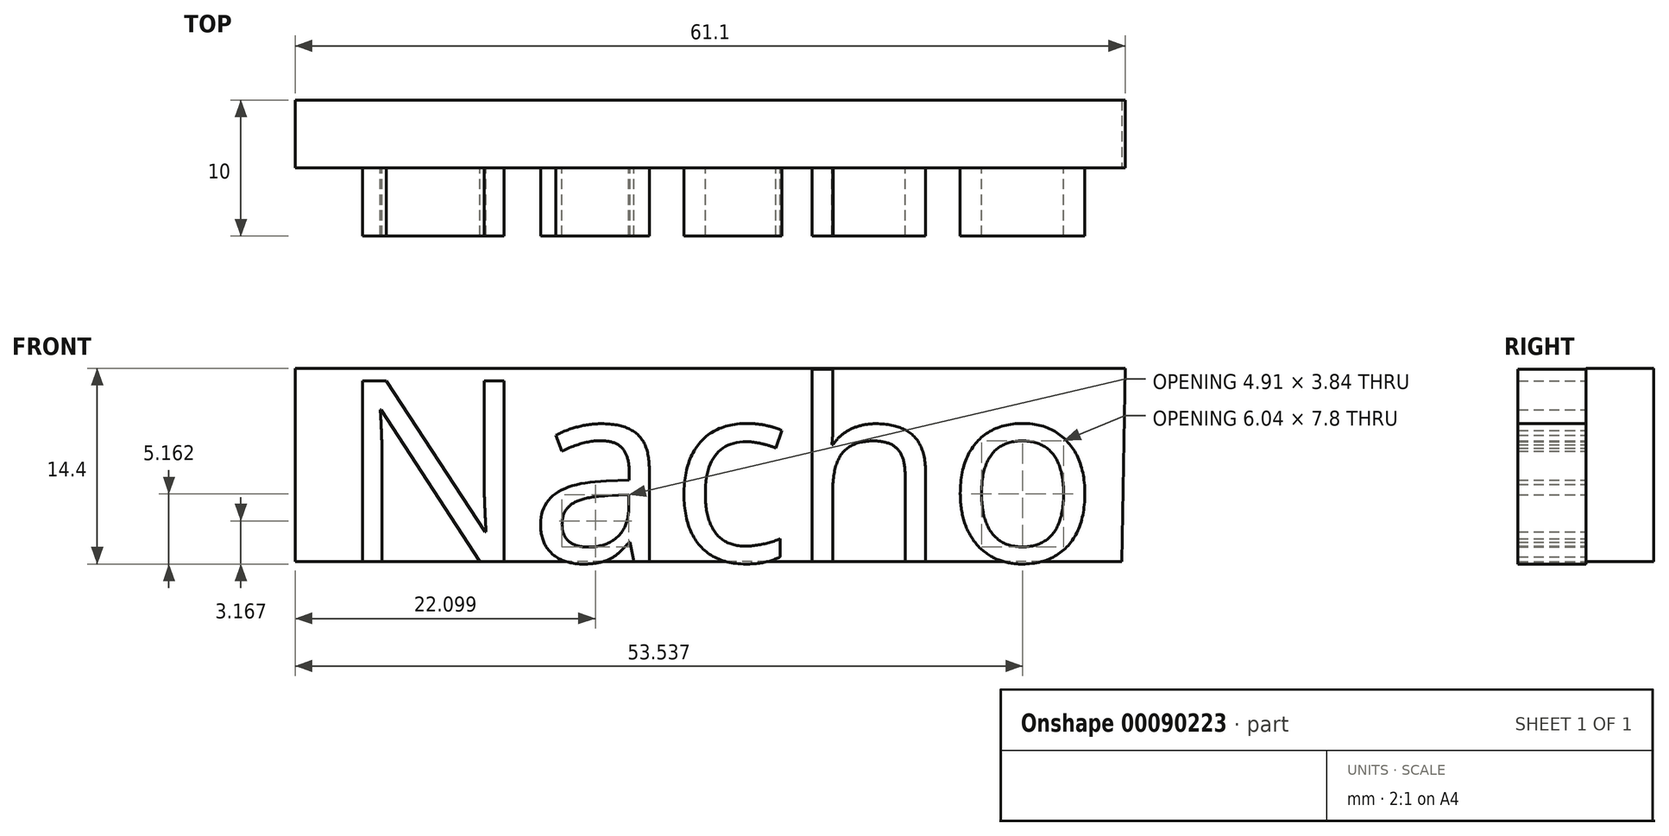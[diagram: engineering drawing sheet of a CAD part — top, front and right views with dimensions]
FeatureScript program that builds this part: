
annotation { "Feature Type Name" : "Feature", "Feature Type Description" : "" }
export const myFeature = defineFeature(function(context is Context, id is Id, definition is map)
    precondition{}
    {
        {
            var Q0;
            Q0=qCreatedBy(makeId("Front.planeOp"),FACE);
            var sketch = newSketch(context, id + "F0", { "sketchPlane" : qUnion([Q0])});
            skText(sketch, "E0", { "text": "Nacho\n", "fontName": "OpenSans-Regular.ttf"});
            const initialGuessF0  = {"E0": [-0.0274, 0, 1, 0, 0.01343]};
            skSetInitialGuess(sketch, initialGuessF0);
            skSolve(sketch);
        }
        {
            var Q0;
            Q0 = qSketchRegion(id + "F0", true);
            extrude(context, id + "F1", {"entities" : qUnion([Q0]), "depth" : 5 * mm});
        }
        {
            var Q0;
            Q0=qCreatedBy(makeId("Front.planeOp"),FACE);
            var sketch = newSketch(context, id + "F2", { "sketchPlane" : qUnion([Q0])});
            skLineSegment(sketch, "E1", {"start": v(30.3, 0) * mm, "end": v(-30.54, 0) * mm});
            skLineSegment(sketch, "E2", {"start": v(-30.54, 0) * mm, "end": v(-30.54, 14.22) * mm});
            skLineSegment(sketch, "E3", {"start": v(-30.54, 14.22) * mm, "end": v(30.56, 14.22) * mm});
            skLineSegment(sketch, "E4", {"start": v(30.3, 0) * mm, "end": v(30.56, 14.22) * mm});
            skSolve(sketch);
        }
        {
            var Q0;
            Q0=makeQuery(id+"F2.imprint","IMPRINT",FACE,{"disambiguationData":[TD([[makeQuery(id+"F2.imprint","IMPRINT",EDGE,{"derivedFrom":sQuery(id+"F2.wireOp",EDGE,"E1")}),-1.0]])]});
            extrude(context, id + "F3", {"entities" : qUnion([Q0]), "oppositeDirection" : true, "depth" : 5 * mm});
        }
    });
